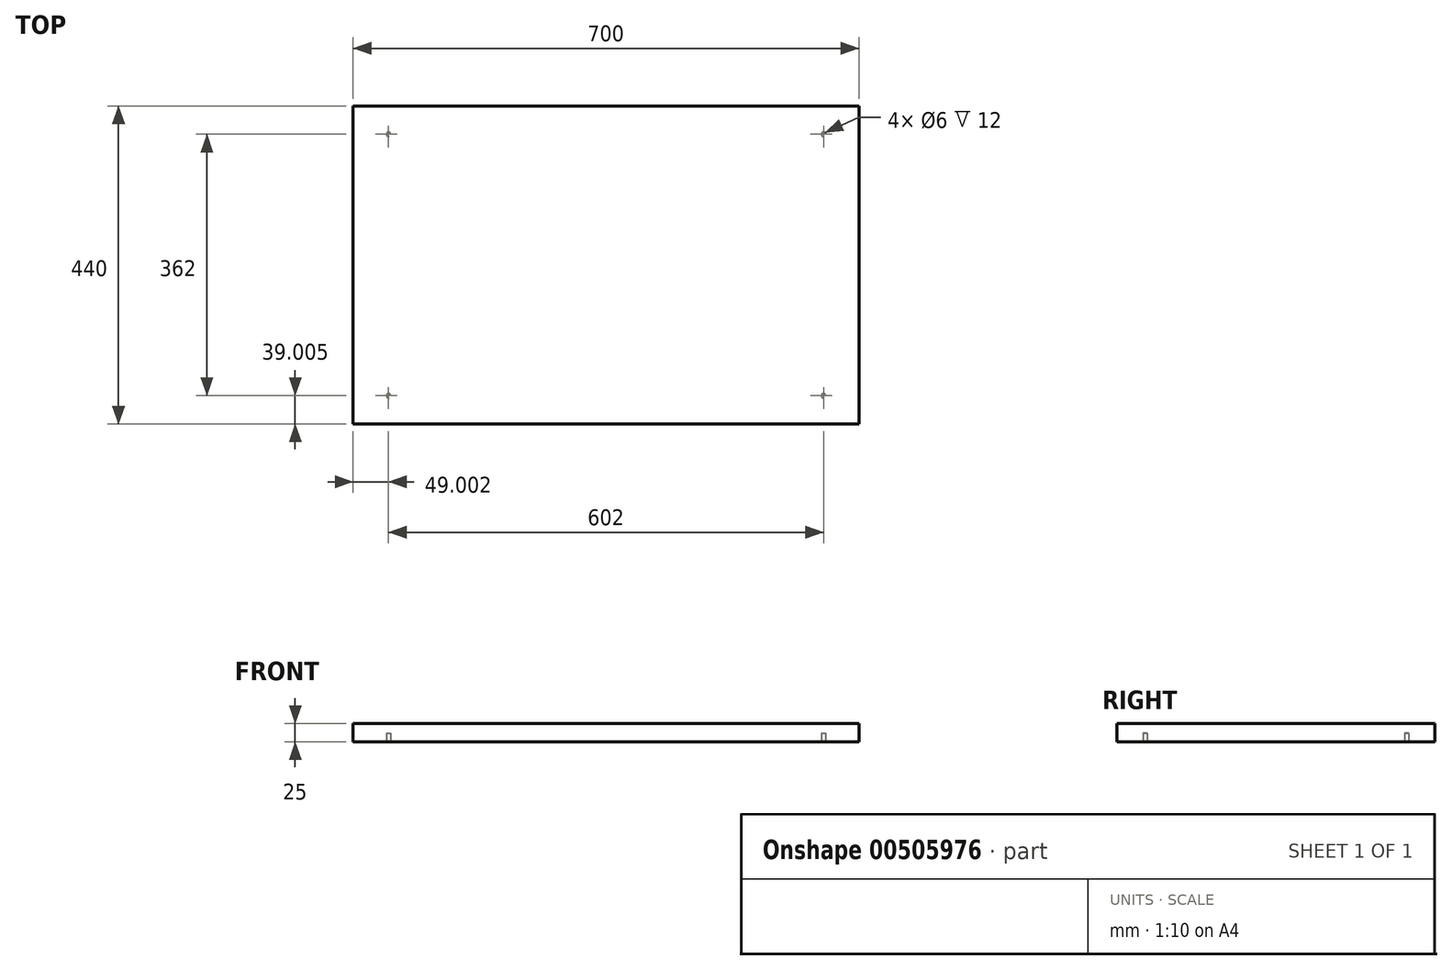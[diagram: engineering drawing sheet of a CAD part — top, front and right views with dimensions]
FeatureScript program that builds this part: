
annotation { "Feature Type Name" : "Feature", "Feature Type Description" : "" }
export const myFeature = defineFeature(function(context is Context, id is Id, definition is map)
    precondition{}
    {
        {
            var Q0;
            Q0=qCreatedBy(makeId("Top.planeOp"),FACE);
            var sketch = newSketch(context, id + "F0", { "sketchPlane" : qUnion([Q0])});
            skLineSegment(sketch, "E0.bottom", {"start": v(-373.6, 383.92) * mm, "end": v(326.4, 383.92) * mm});
            skLineSegment(sketch, "E0.top", {"start": v(-373.6, -56.08) * mm, "end": v(326.4, -56.08) * mm});
            skLineSegment(sketch, "E0.left", {"start": v(-373.6, 383.92) * mm, "end": v(-373.6, -56.08) * mm});
            skLineSegment(sketch, "E0.right", {"start": v(326.4, 383.92) * mm, "end": v(326.4, -56.08) * mm});
            skSolve(sketch);
        }
        {
            var Q0;
            Q0 = qSketchRegion(id + "F0", true);
            extrude(context, id + "F1", {"entities" : qUnion([Q0]), "depth" : 25 * mm, "offsetDistance" : 25 * mm});
        }
        {
            var Q0;
            Q0=makeQuery(id+"F1.opExtrude","CAP_FACE",FACE,{"disambiguationData":[OSD([sQuery(id+"F0.wireOp",EDGE,"E0.bottom"),sQuery(id+"F0.wireOp",EDGE,"E0.top"),sQuery(id+"F0.wireOp",EDGE,"E0.left"),sQuery(id+"F0.wireOp",EDGE,"E0.right")])],"isStart":true});
            var sketch = newSketch(context, id + "F2", { "sketchPlane" : qUnion([Q0])});
            skCircle(sketch, "E1", {"center": v(277.4, 17.08) * mm, "radius": 3 * mm});
            skCircle(sketch, "E2", {"center": v(-324.6, 17.08) * mm, "radius": 3 * mm});
            skCircle(sketch, "E3", {"center": v(-324.6, -344.92) * mm, "radius": 3 * mm});
            skCircle(sketch, "E4", {"center": v(277.4, -344.92) * mm, "radius": 3 * mm});
            skSolve(sketch);
        }
        {
            var Q0;
            Q0=makeQuery(id+"F2.imprint","IMPRINT",FACE,{"disambiguationData":[TD([[makeQuery(id+"F2.imprint","IMPRINT",EDGE,{"derivedFrom":sQuery(id+"F2.wireOp",EDGE,"E1")}),1.0]])]});
            var Q1;
            Q1=makeQuery(id+"F2.imprint","IMPRINT",FACE,{"disambiguationData":[TD([[makeQuery(id+"F2.imprint","IMPRINT",EDGE,{"derivedFrom":sQuery(id+"F2.wireOp",EDGE,"E3")}),1.0]])]});
            var Q2;
            Q2=makeQuery(id+"F2.imprint","IMPRINT",FACE,{"disambiguationData":[TD([[makeQuery(id+"F2.imprint","IMPRINT",EDGE,{"derivedFrom":sQuery(id+"F2.wireOp",EDGE,"E4")}),1.0]])]});
            var Q3;
            Q3=makeQuery(id+"F2.imprint","IMPRINT",FACE,{"disambiguationData":[TD([[makeQuery(id+"F2.imprint","IMPRINT",EDGE,{"derivedFrom":sQuery(id+"F2.wireOp",EDGE,"E2")}),1.0]])]});
            extrude(context, id + "F3", {"entities" : qUnion([Q0, Q1, Q2, Q3]), "operationType" : NewBodyOperationType.REMOVE, "oppositeDirection" : true, "depth" : 12 * mm, "offsetDistance" : 25 * mm});
        }
    });
